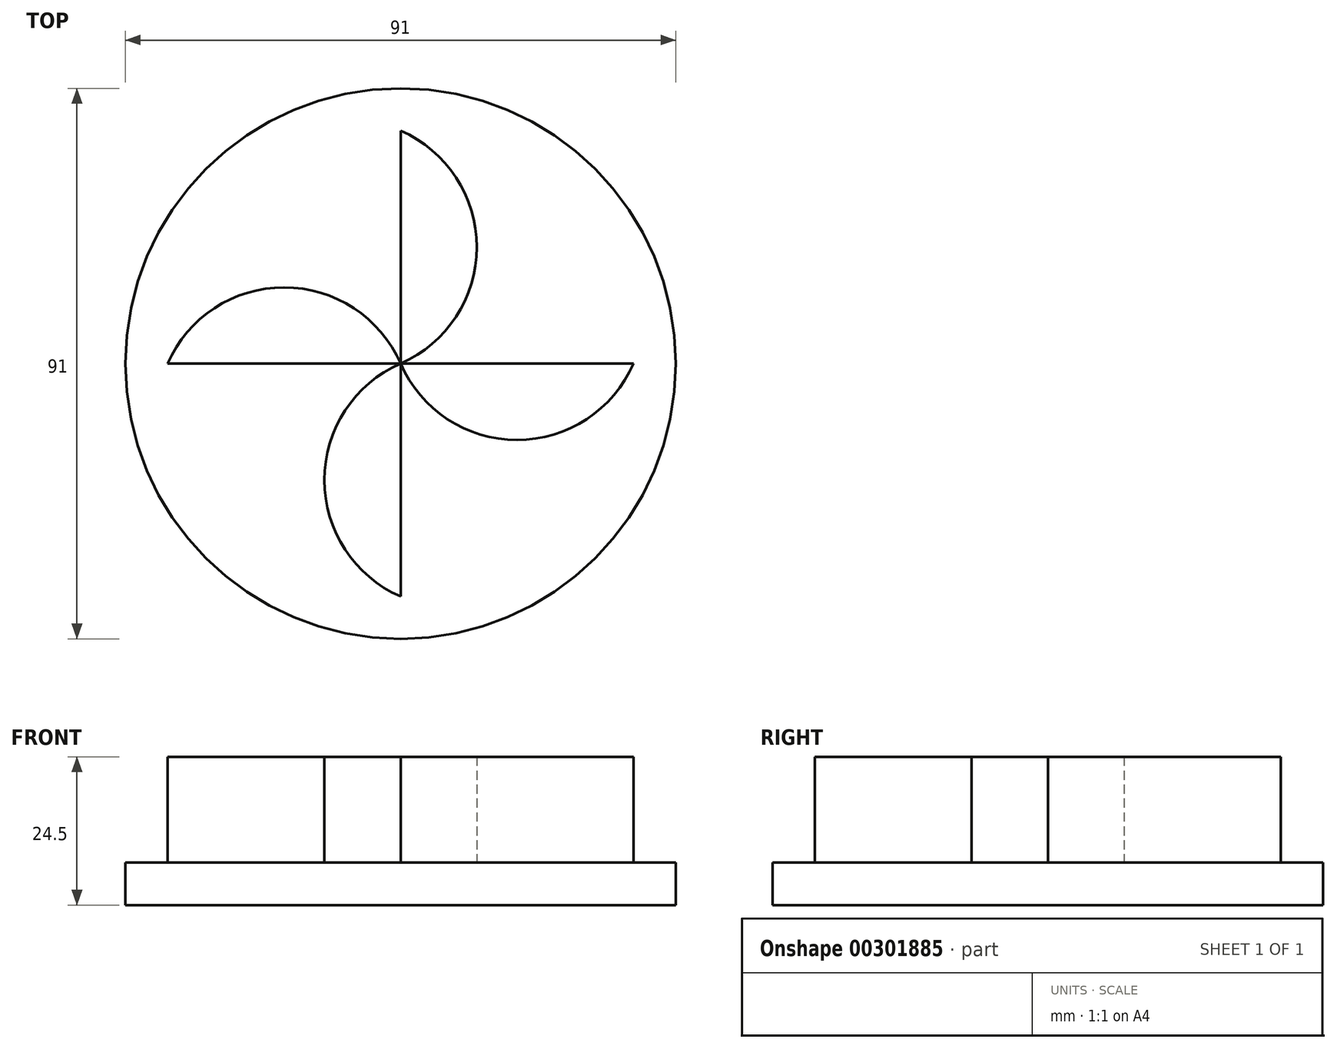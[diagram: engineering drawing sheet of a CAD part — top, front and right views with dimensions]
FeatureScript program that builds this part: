
annotation { "Feature Type Name" : "Feature", "Feature Type Description" : "" }
export const myFeature = defineFeature(function(context is Context, id is Id, definition is map)
    precondition{}
    {
        {
            var Q0;
            Q0=qCreatedBy(makeId("Top.planeOp"),FACE);
            var sketch = newSketch(context, id + "F0", { "sketchPlane" : qUnion([Q0])});
            skCircle(sketch, "E0", {"center": v(0, 0) * mm, "radius": 65 * mm});
            skSolve(sketch);
        }
        {
            var Q0;
            Q0=qSketchRegion(id+"F0",true);
            extrude(context, id + "F1", {"entities" : qUnion([Q0]), "depth" : 10 * mm});
        }
        {
            var Q0;
            Q0=makeQuery(id+"F1.opExtrude","CAP_FACE",FACE,{"disambiguationData":[OSD([sQuery(id+"F0.wireOp",EDGE,"E0")])],"isStart":false});
            var sketch = newSketch(context, id + "F2", { "sketchPlane" : qUnion([Q0])});
            skArc(sketch, "E1", {"start": v(0, 0) * mm, "mid": v(18.01, 27.5) * mm, "end": v(0, 55) * mm});
            skArc(sketch, "E2", {"start": v(0, 0) * mm, "mid": v(27.5, -18.01) * mm, "end": v(55, 0) * mm});
            skArc(sketch, "E3", {"start": v(0, 0) * mm, "mid": v(-18.01, -27.5) * mm, "end": v(0, -55) * mm});
            skArc(sketch, "E4", {"start": v(0, 0) * mm, "mid": v(-27.5, 18.01) * mm, "end": v(-55, 0) * mm});
            skLineSegment(sketch, "E5", {"start": v(0, 55) * mm, "end": v(0, 0) * mm});
            skLineSegment(sketch, "E6", {"start": v(-55, 0) * mm, "end": v(0, 0) * mm});
            skLineSegment(sketch, "E7", {"start": v(0, -55) * mm, "end": v(0, 0) * mm});
            skLineSegment(sketch, "E8", {"start": v(0, 0) * mm, "end": v(55, 0) * mm});
            skSolve(sketch);
        }
        {
            var Q0;
            Q0=qSketchRegion(id+"F2",true);
            extrude(context, id + "F3", {"entities" : qUnion([Q0]), "depth" : 25 * mm});
        }
        {
            var Q0;
            Q0=makeQuery(id+"F1.opExtrude","SWEPT_BODY",BODY,{"disambiguationData":[OSD([sQuery(id+"F0.wireOp",EDGE,"E0")])]});
            var Q1;
            Q1=makeQuery(id+"F3.opExtrude","SWEPT_BODY",BODY,{"disambiguationData":[OSD([sQuery(id+"F2.wireOp",EDGE,"E1"),sQuery(id+"F2.wireOp",EDGE,"E5")])]});
            var Q2;
            Q2=makeQuery(id+"F3.opExtrude","SWEPT_BODY",BODY,{"disambiguationData":[OSD([sQuery(id+"F2.wireOp",EDGE,"E2"),sQuery(id+"F2.wireOp",EDGE,"E8")])]});
            var Q3;
            Q3=makeQuery(id+"F3.opExtrude","SWEPT_BODY",BODY,{"disambiguationData":[OSD([sQuery(id+"F2.wireOp",EDGE,"E3"),sQuery(id+"F2.wireOp",EDGE,"E7")])]});
            var Q4;
            Q4=makeQuery(id+"F3.opExtrude","SWEPT_BODY",BODY,{"disambiguationData":[OSD([sQuery(id+"F2.wireOp",EDGE,"E4"),sQuery(id+"F2.wireOp",EDGE,"E6")])]});
            var Q5;
            Q5=qCreatedBy(makeId("Origin.pointOp"),VERTEX);
            transform(context, id + "F4", {"entities" : qUnion([Q0, Q1, Q2, Q3, Q4]), "transformType" : TransformType.SCALE_UNIFORMLY, "scale" : 0.7, "scalePoint" : qUnion([Q5]), "makeCopy" : false});
        }
    });
